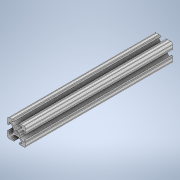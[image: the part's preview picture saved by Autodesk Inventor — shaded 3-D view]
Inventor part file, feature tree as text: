
AUTODESK INVENTOR PART (.ipt)
format: ipt  version: 2020 (Build 240168000, 168)  size: 233,472 bytes
history: native  units: in
note: dims shown in document units (in); Inventor stores cm internally (conversion verified against a paired STEP export)
features: extrude x1, sketch x1
ambient origin geometry x8: Origin, YZ Plane, XZ Plane, XY Plane, X Axis, Y Axis, Z Axis, Center Point
bodies: Solid1 (feature_tree)
feature tree (2):
  extrude  "Extrusion1"  [1 undecoded]
  sketch  "Sketch1"  dims[d0=8.0in d1=0.0in]
note: 1 required parameter value undecoded (feature->parameter linkage not recoverable at this tier; creation-order binding heuristic only, values carry confidence <= 0.55)
